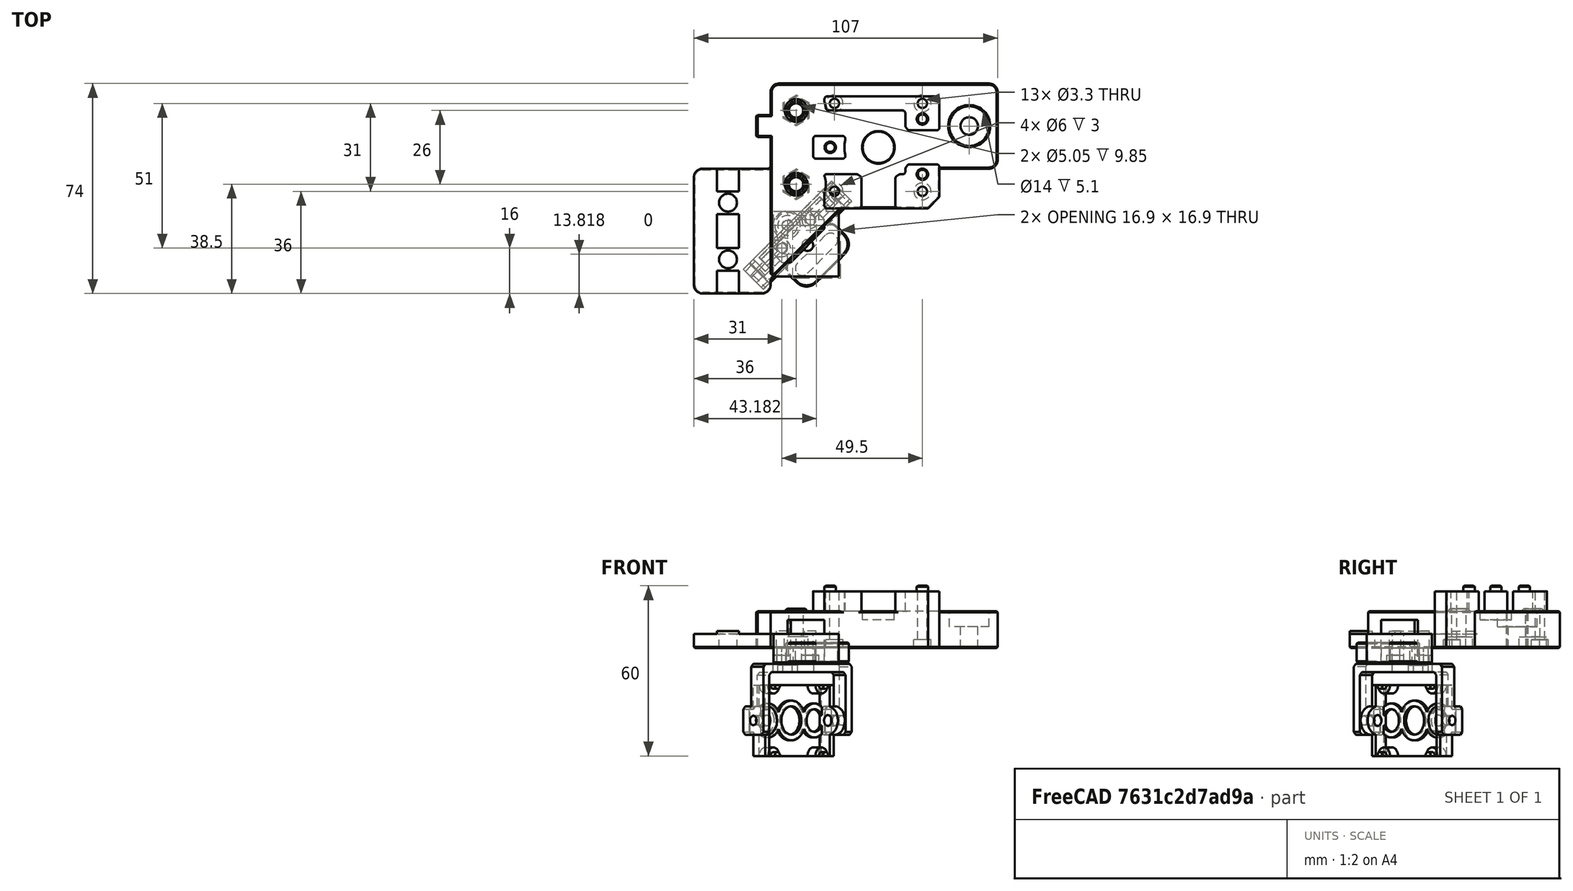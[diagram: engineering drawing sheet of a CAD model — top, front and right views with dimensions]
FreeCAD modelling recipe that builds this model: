
FCSTD DOCUMENT  (FreeCAD 0.18R16146 (Git))
Label: motor-mount-plugin
License: Other
LicenseURL: GPL3
objects: Part::Feature×9, Part::Cylinder×7, Part::Box×6, Part::MultiFuse×5, Part::Cut×5, Part::Chamfer×3, Part::Fillet×3, App::Part×1
note: 38 computed .brp shape members not serialized (recipe doc carries the construction recipe); baked Part::Feature solids carry a one-line shape summary decoded from their .brp

FEATURE [Part::Feature] Cut002008023012009006003002001  label="mounter-template"
  Placement = pos=(-13,27,10) rot=(0,0,1;0rad)
  shape: bbox 18 x 18 x 5 mm, 12 faces (baked)
FEATURE [Part::Box] Box  label="Cube"
  AttacherType = Attacher::AttachEngine3D
  Height = 10
  Length = 13
  Placement = pos=(-7,-6,5) rot=(0,0,1;0rad)
  Width = 13
FEATURE [Part::Cylinder] Cylinder
  Angle = 360
  AttacherType = Attacher::AttachEngine3D
  Height = 10
  Radius = 2
FEATURE [Part::Feature] Chamfer043001  label="motor-mount"
  Placement = pos=(-13,27,10) rot=(0,0,1;0rad)
  shape: bbox 107 x 74 x 22 mm, 206 faces (baked)
FEATURE [Part::Chamfer] Chamfer
  Base = -> Box
  Edges = 1 edges r=11.85: [Edge5]
FEATURE [Part::Box] Box001  label="Cube001"
  AttacherType = Attacher::AttachEngine3D
  Height = 10
  Length = 23
  Placement = pos=(-12,-11,0) rot=(0,0,1;0rad)
  Width = 23
FEATURE [Part::Feature] Cut002008023012009006003002002  label="mounter-template001"
  Placement = pos=(-13,27,10) rot=(0,0,1;0rad)
  shape: bbox 18 x 18 x 5 mm, 12 faces (baked)
FEATURE [Part::Box] Box002  label="Cube002"
  AttacherType = Attacher::AttachEngine3D
  Height = 7
  Length = 24
  Placement = pos=(-12,0,0) rot=(0,0,1;0rad)
  Width = 12
FEATURE [Part::Cylinder] Cylinder001
  Angle = 360
  AttacherType = Attacher::AttachEngine3D
  Height = 10
  Placement = pos=(-7,5,0) rot=(0,0,1;0rad)
  Radius = 2.5
FEATURE [Part::Cylinder] Cylinder002
  Angle = 360
  AttacherType = Attacher::AttachEngine3D
  Height = 10
  Placement = pos=(7,5,0) rot=(0,0,1;0rad)
  Radius = 2.5
FEATURE [Part::Box] Box003  label="Cube003"
  AttacherType = Attacher::AttachEngine3D
  Height = 10
  Length = 14
  Placement = pos=(-7,2.5,0) rot=(0,0,1;0rad)
  Width = 5
FEATURE [Part::MultiFuse] Fusion
  Shapes = -> [Cylinder001,Box003,Cylinder002]
FEATURE [Part::Cut] Cut
  Base = -> Box002
  Tool = -> Fusion
FEATURE [Part::Fillet] Fillet
  Base = -> Cut
  Edges = 2 edges r=3: [Edge1,Edge6]
FEATURE [Part::Fillet] Fillet001
  Base = -> Fillet
  Edges = 10 edges r=1: [Edge10,Edge11,Edge12,Edge13,Edge14,Edge22,Edge23,Edge24,Edge25,Edge26]
FEATURE [Part::Fillet] Fillet002
  Base = -> Fillet001
  Edges = 2 edges r=5: [Edge23,Edge28]
FEATURE [Part::Chamfer] Chamfer043002
  Base = -> Fillet002
  Edges = 16 edges r=0.4: [Edge1,Edge2,Edge3,Edge4,Edge5,Edge6,Edge7,Edge8,Edge16,Edge17,Edge19,Edge21,Edge23,Edge25,Edge27,Edge29]
  Placement = pos=(-0.353553,0.353553,0) rot=(0,0,1;3.92699rad)
FEATURE [Part::MultiFuse] Fusion001  label="TPFE-tube-guide"
  Shapes = -> [Cut002008023012009006003002002,Chamfer043002]
FEATURE [Part::Feature] Fusion001001  label="TPFE-tube-guide001"
  shape: bbox 26.55 x 26.55 x 7 mm, 51 faces (baked)
FEATURE [Part::Feature] Chamfer004001  label="Chamfer007"
  Placement = pos=(-7.07107,7.07107,-20.5) rot=(0.862856,0.357407,0.357407;1.71777rad)
  shape: bbox 38.18 x 38.18 x 25 mm, 67 faces (baked)
FEATURE [Part::Feature] Cut003002  label="Cut005"
  Placement = pos=(-7.07107,7.07107,-20.5) rot=(0.862856,0.357407,0.357407;1.71777rad)
  shape: bbox 33.45 x 33.45 x 25 mm, 128 faces (baked)
FEATURE [Part::Feature] Cut002008023012009006003002003  label="mounter-template002"
  Placement = pos=(-13,27,10) rot=(0,0,1;0rad)
  shape: bbox 18 x 18 x 5 mm, 12 faces (baked)
FEATURE [Part::Cylinder] Cylinder003
  Angle = 360
  AttacherType = Attacher::AttachEngine3D
  Height = 2.5
  Placement = pos=(-9,-1,0) rot=(0,0,1;0rad)
  Radius = 3
FEATURE [Part::Cylinder] Cylinder004
  Angle = 360
  AttacherType = Attacher::AttachEngine3D
  Height = 2.5
  Placement = pos=(1,9,0) rot=(0,0,1;0rad)
  Radius = 3
FEATURE [Part::MultiFuse] Fusion001002
  Shapes = -> [Cylinder003,Cylinder004]
FEATURE [Part::Cut] Cut002008023012009006003002004
  Base = -> Cut002008023012009006003002003
  Tool = -> Fusion001002
FEATURE [Part::Cylinder] Cylinder005
  Angle = 360
  AttacherType = Attacher::AttachEngine3D
  Height = 6
  Placement = pos=(-7,7,-1) rot=(0,0,1;0rad)
  Radius = 2
FEATURE [Part::Cylinder] Cylinder006
  Angle = 360
  AttacherType = Attacher::AttachEngine3D
  Height = 6
  Placement = pos=(-7,7,-1) rot=(0,0,1;0rad)
  Radius = 4.5
FEATURE [Part::Chamfer] Chamfer043003
  Base = -> Cylinder006
  Edges = 1 edges r=1: [Edge3]
FEATURE [Part::MultiFuse] Fusion001003
  Shapes = -> [Cut002008023012009006003002004,Chamfer043003]
FEATURE [Part::Cut] Cut002008023012009006003002005
  Base = -> Fusion001003
  Tool = -> Cylinder005
FEATURE [Part::Box] Box004  label="Cube004"
  AttacherType = Attacher::AttachEngine3D
  Height = 2.5
  Length = 6
  Placement = pos=(-2,9,0) rot=(0,0,1;0rad)
  Width = 3
FEATURE [Part::Box] Box005  label="Cube005"
  AttacherType = Attacher::AttachEngine3D
  Height = 2.5
  Length = 3
  Placement = pos=(-12,-4,0) rot=(0,0,1;0rad)
  Width = 6
FEATURE [Part::MultiFuse] Fusion001004
  Shapes = -> [Box004,Box005]
FEATURE [Part::Feature] Box006001  label="Cube007"
  Placement = pos=(-0.707107,0.707107,0) rot=(0,0,1;3.92699rad)
  shape: bbox 28.28 x 28.28 x 10 mm, 6 faces (baked)
FEATURE [Part::Cut] Cut002008023012009006003002006
  Base = -> Cut002008023012009006003002005
  Tool = -> Fusion001004
FEATURE [Part::Cut] Cut002008023012009006003002007  label="camera-mount-base"
  Base = -> Cut002008023012009006003002006
  Tool = -> Box006001
FEATURE [Part::Feature] Cut002008023012009006003002007001  label="camera-mount-base001"
  shape: bbox 18 x 18 x 6 mm, 23 faces (baked)
FEATURE [App::Part] Part  label="camera-mount002"
  Group = -> [Cut003002,Chamfer004001,Cut002008023012009006003002007001]
  Origin = -> Origin
